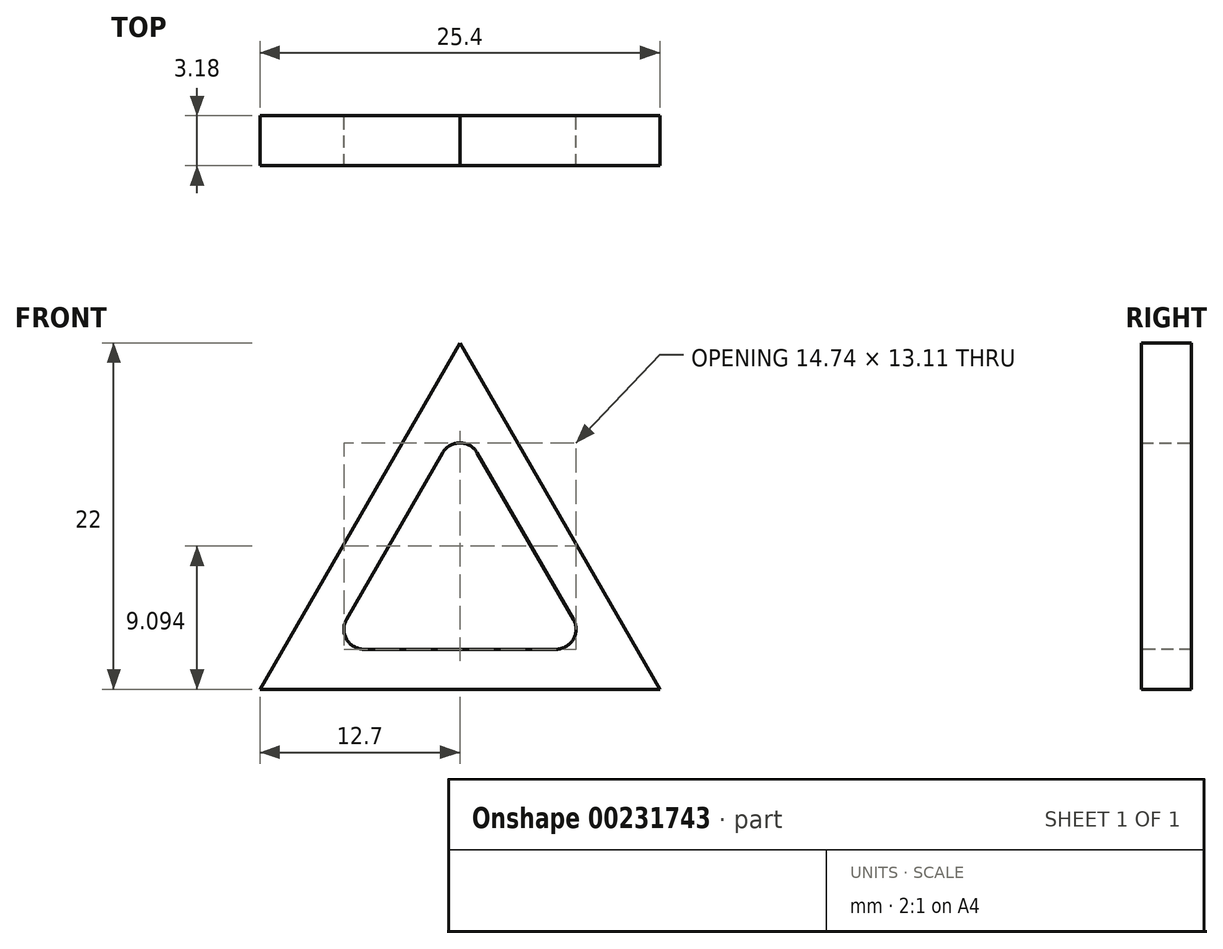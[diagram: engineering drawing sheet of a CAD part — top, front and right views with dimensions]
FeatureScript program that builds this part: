
annotation { "Feature Type Name" : "Feature", "Feature Type Description" : "" }
export const myFeature = defineFeature(function(context is Context, id is Id, definition is map)
    precondition{}
    {
        {
            var Q0;
            Q0=qCreatedBy(makeId("Front.planeOp"),FACE);
            var sketch = newSketch(context, id + "F0", { "sketchPlane" : qUnion([Q0])});
            skLineSegment(sketch, "E0", {"start": v(0, 22) * mm, "end": v(-12.7, 0) * mm});
            skLineSegment(sketch, "E1", {"start": v(0, 22) * mm, "end": v(12.7, 0) * mm});
            skLineSegment(sketch, "E2", {"start": v(-12.7, 0) * mm, "end": v(12.7, 0) * mm});
            skSolve(sketch);
        }
        {
            var Q0;
            Q0=qSketchRegion(id+"F0",true);
            extrude(context, id + "F1", {"entities" : qUnion([Q0]), "endBound" : BoundingType.SYMMETRIC, "depth" : 3.17 * mm});
        }
        {
            var Q0;
            Q0=makeQuery(id+"F1.opExtrude","CAP_FACE",FACE,{"disambiguationData":[OSD([sQuery(id+"F0.wireOp",EDGE,"E0"),sQuery(id+"F0.wireOp",EDGE,"E1"),sQuery(id+"F0.wireOp",EDGE,"E2")])],"isStart":false});
            var sketch = newSketch(context, id + "F2", { "sketchPlane" : qUnion([Q0])});
            skLineSegment(sketch, "E3", {"start": v(0, 16.92) * mm, "end": v(-8.3, 2.54) * mm});
            skLineSegment(sketch, "E4", {"start": v(-8.3, 2.54) * mm, "end": v(8.3, 2.54) * mm});
            skLineSegment(sketch, "E5", {"start": v(8.3, 2.54) * mm, "end": v(0, 16.92) * mm});
            skSolve(sketch);
        }
        {
            var Q0;
            Q0=qSketchRegion(id+"F2",true);
            extrude(context, id + "F3", {"entities" : qUnion([Q0]), "operationType" : NewBodyOperationType.REMOVE, "endBound" : BoundingType.THROUGH_ALL, "oppositeDirection" : true, "depth" : 25.4 * mm});
        }
        {
            var Q0;
            Q0=makeQuery(id+"F3.boolean.opBoolean","COPY",EDGE,{"derivedFrom":makeQuery(id+"F3.opExtrude","SWEPT_EDGE",EDGE,{"disambiguationData":[OSD([sQuery(id+"F2.wireOp",EDGE,"E3"),sQuery(id+"F2.wireOp",EDGE,"E5")])]})});
            var Q1;
            Q1=makeQuery(id+"F3.boolean.opBoolean","COPY",EDGE,{"derivedFrom":makeQuery(id+"F3.opExtrude","SWEPT_EDGE",EDGE,{"disambiguationData":[OSD([sQuery(id+"F2.wireOp",EDGE,"E4"),sQuery(id+"F2.wireOp",EDGE,"E5")])]})});
            var Q2;
            Q2=makeQuery(id+"F3.boolean.opBoolean","COPY",EDGE,{"derivedFrom":makeQuery(id+"F3.opExtrude","SWEPT_EDGE",EDGE,{"disambiguationData":[OSD([sQuery(id+"F2.wireOp",EDGE,"E3"),sQuery(id+"F2.wireOp",EDGE,"E4")])]})});
            fillet(context, id + "F4", {"entities" : qUnion([Q0, Q1, Q2]), "radius" : 1.27 * mm, "tangentPropagation" : true, "allowEdgeOverflow" : false});
        }
    });
